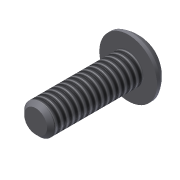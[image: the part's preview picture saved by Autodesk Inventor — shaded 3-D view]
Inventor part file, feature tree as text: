
AUTODESK INVENTOR PART (.ipt)
format: ipt  version: 2013 (Build 170138000, 138)  size: 120,832 bytes
history: native  units: in
note: dims shown in document units (in); Inventor stores cm internally (conversion verified against a paired STEP export)
features: sketch x3, extrude x2, revolve x1, chamfer x1, thread x1
ambient origin geometry x8: Origin, YZ Plane, XZ Plane, XY Plane, X Axis, Y Axis, Z Axis, Center Point
bodies: Solid1 (feature_tree)
feature tree (8):
  extrude  "Extrusion1"  Depth=0.5in TaperAngle=0.0deg
  revolve  "Revolution1"  [1 undecoded]
  extrude  "Extrusion2"  Depth=0.0938in
  chamfer  "Chamfer1"  Distance=0.0625in
  thread  "Thread1"  [1 undecoded]
  sketch  "Sketch1"  dims[d0=0.164in d1=0.5in d2=0.0in]
  sketch  "Sketch2"  dims[d3=0.087in d6=0.08in]
  sketch  "Sketch3"  dims[d7=90.0deg d8=0.0938in d9=0.0625in d10=0.0in d13=0.02in d14=0.125in d15=45.0deg d16=1.0in d17=0.0in d19=0.156in]
note: 2 required parameter values undecoded (feature->parameter linkage not recoverable at this tier; creation-order binding heuristic only, values carry confidence <= 0.55)